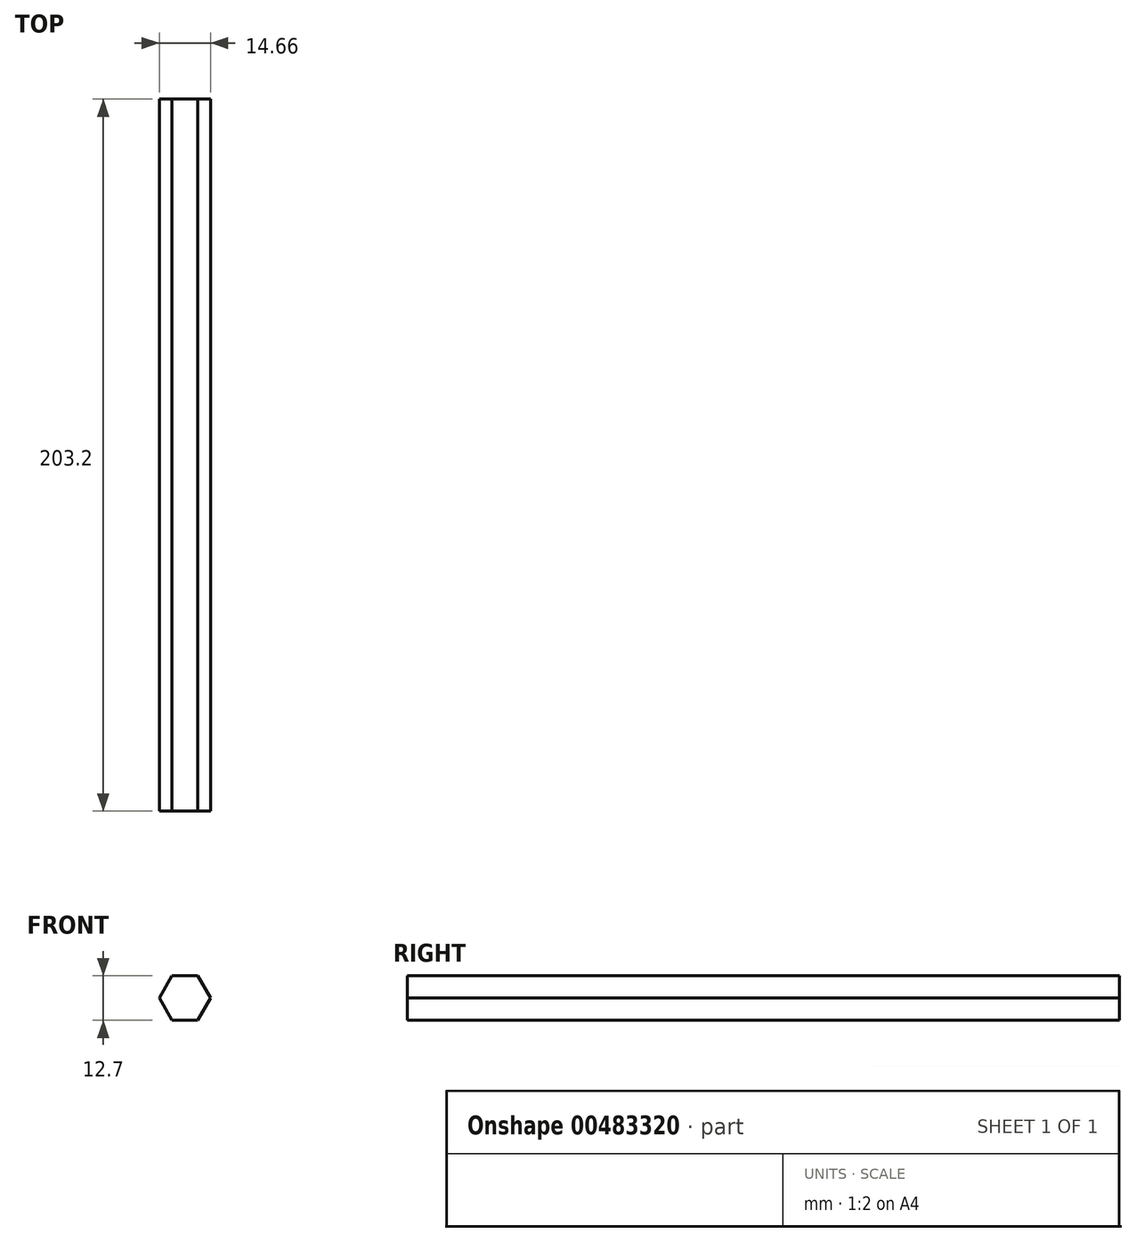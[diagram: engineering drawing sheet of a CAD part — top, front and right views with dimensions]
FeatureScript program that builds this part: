
annotation { "Feature Type Name" : "Feature", "Feature Type Description" : "" }
export const myFeature = defineFeature(function(context is Context, id is Id, definition is map)
    precondition{}
    {
        {
            var Q0;
            Q0=qCreatedBy(makeId("Front.planeOp"),FACE);
            var sketch = newSketch(context, id + "F0", { "sketchPlane" : qUnion([Q0])});
            skCircle(sketch, "E0.cCircle", {"center": v(0, 0) * mm, "radius": 6.35 * mm, "construction": true});
            skLineSegment(sketch, "E0.0", {"start": v(-3.67, 6.35) * mm, "end": v(3.67, 6.35) * mm});
            skLineSegment(sketch, "E0.1", {"start": v(3.67, 6.35) * mm, "end": v(7.33, 0) * mm});
            skLineSegment(sketch, "E0.2", {"start": v(7.33, 0) * mm, "end": v(3.67, -6.35) * mm});
            skLineSegment(sketch, "E0.3", {"start": v(3.67, -6.35) * mm, "end": v(-3.67, -6.35) * mm});
            skLineSegment(sketch, "E0.4", {"start": v(-3.67, -6.35) * mm, "end": v(-7.33, 0) * mm});
            skLineSegment(sketch, "E0.5", {"start": v(-7.33, 0) * mm, "end": v(-3.67, 6.35) * mm});
            skPoint(sketch, "E0.0.midPoint", {"position": v(0, 6.35) * mm});
            skSolve(sketch);
        }
        {
            var Q0;
            Q0 = qSketchRegion(id + "F0", true);
            extrude(context, id + "F1", {"entities" : qUnion([Q0]), "endBound" : BoundingType.SYMMETRIC, "depth" : 203.2 * mm});
        }
    });
